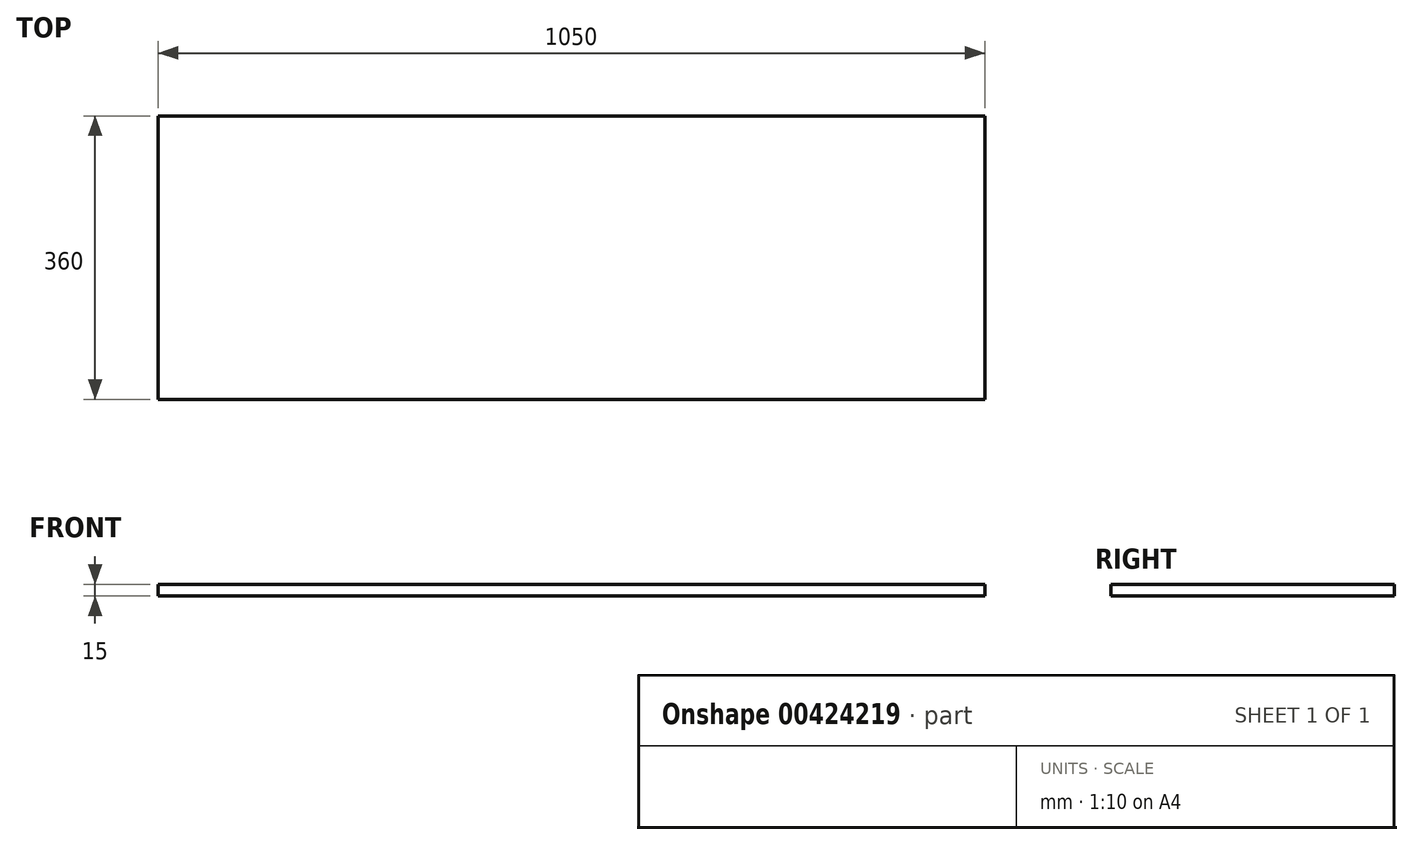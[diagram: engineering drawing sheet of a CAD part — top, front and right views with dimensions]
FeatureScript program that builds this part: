
annotation { "Feature Type Name" : "Feature", "Feature Type Description" : "" }
export const myFeature = defineFeature(function(context is Context, id is Id, definition is map)
    precondition{}
    {
        {
            var Q0;
            Q0=qCreatedBy(makeId("Top.planeOp"),FACE);
            var sketch = newSketch(context, id + "F0", { "sketchPlane" : qUnion([Q0])});
            skLineSegment(sketch, "E0.bottom", {"start": v(-518.94, -3.68) * mm, "end": v(531.06, -3.68) * mm});
            skLineSegment(sketch, "E0.top", {"start": v(-518.94, -363.68) * mm, "end": v(531.06, -363.68) * mm});
            skLineSegment(sketch, "E0.left", {"start": v(-518.94, -3.68) * mm, "end": v(-518.94, -363.68) * mm});
            skLineSegment(sketch, "E0.right", {"start": v(531.06, -3.68) * mm, "end": v(531.06, -363.68) * mm});
            skSolve(sketch);
        }
        {
            var Q0;
            Q0 = qSketchRegion(id + "F0", true);
            extrude(context, id + "F1", {"entities" : qUnion([Q0]), "depth" : 15 * mm});
        }
    });
